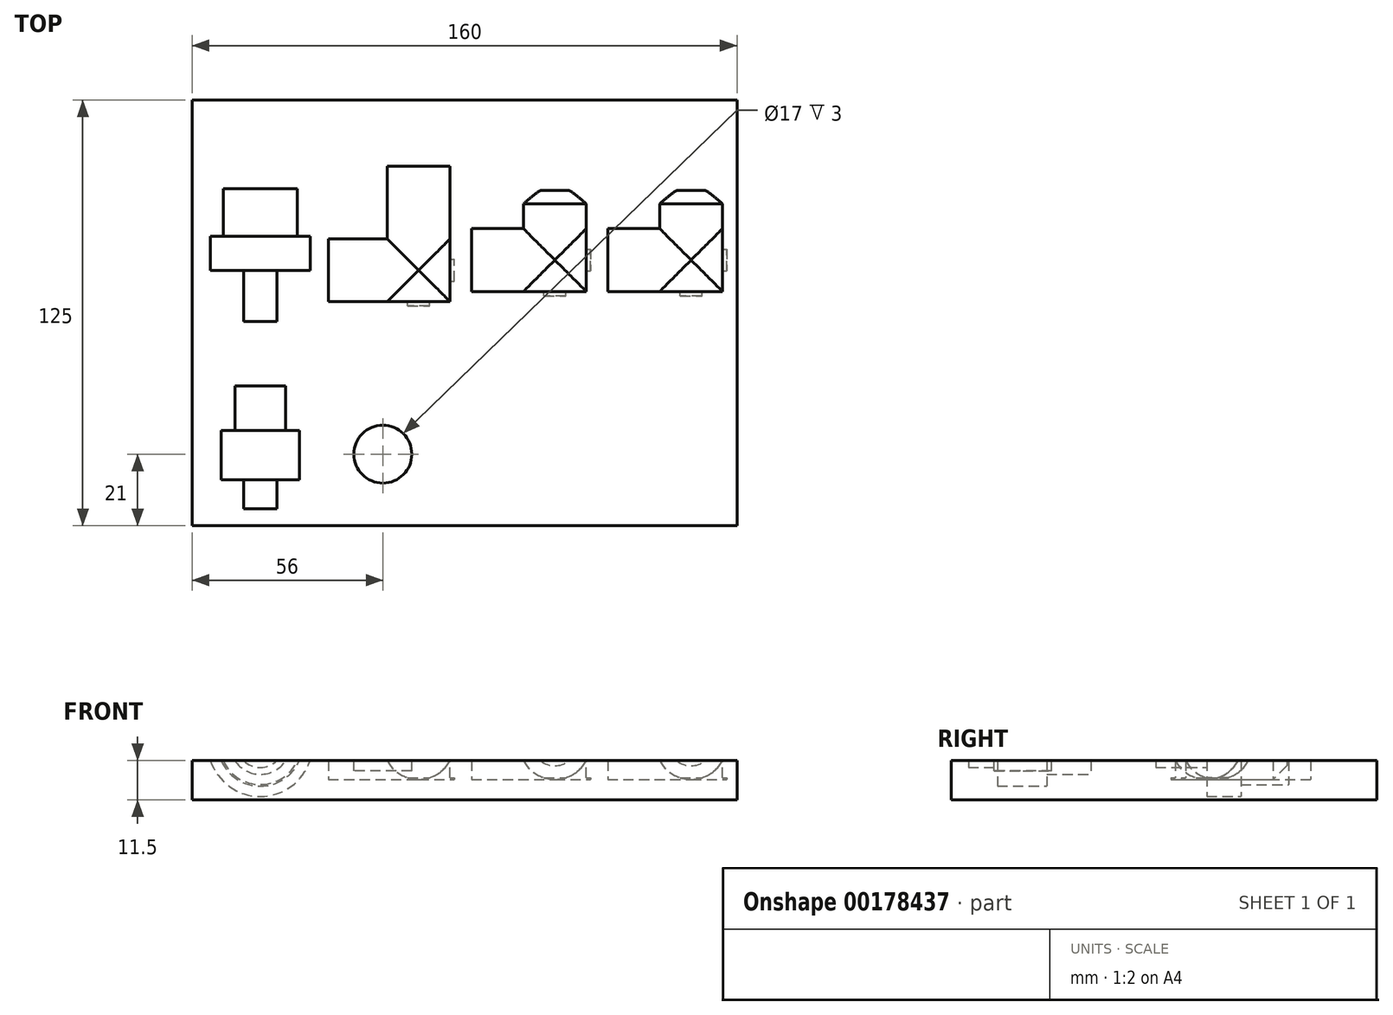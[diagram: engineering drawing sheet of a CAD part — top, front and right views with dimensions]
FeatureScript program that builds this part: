
annotation { "Feature Type Name" : "Feature", "Feature Type Description" : "" }
export const myFeature = defineFeature(function(context is Context, id is Id, definition is map)
    precondition{}
    {
        {
            var Q0;
            Q0=qCreatedBy(makeId("Top.planeOp"),FACE);
            var sketch = newSketch(context, id + "F0", { "sketchPlane" : qUnion([Q0])});
            skLineSegment(sketch, "E0.bottom", {"start": v(0, 0) * mm, "end": v(160, 0) * mm});
            skLineSegment(sketch, "E0.top", {"start": v(0, 125) * mm, "end": v(160, 125) * mm});
            skLineSegment(sketch, "E0.left", {"start": v(0, 0) * mm, "end": v(0, 125) * mm});
            skLineSegment(sketch, "E0.right", {"start": v(160, 0) * mm, "end": v(160, 125) * mm});
            skSolve(sketch);
        }
        {
            var Q0;
            Q0=makeQuery(id+"F0.imprint","IMPRINT",FACE,{"disambiguationData":[TD([[makeQuery(id+"F0.imprint","IMPRINT",EDGE,{"derivedFrom":sQuery(id+"F0.wireOp",EDGE,"E0.bottom")}),1.0]])]});
            extrude(context, id + "F1", {"entities" : qUnion([Q0]), "oppositeDirection" : true, "depth" : 16.5 * mm});
        }
        {
            var Q0;
            Q0=makeQuery(id+"F1.opExtrude","CAP_FACE",FACE,{"disambiguationData":[OSD([sQuery(id+"F0.wireOp",EDGE,"E0.bottom"),sQuery(id+"F0.wireOp",EDGE,"E0.top"),sQuery(id+"F0.wireOp",EDGE,"E0.left"),sQuery(id+"F0.wireOp",EDGE,"E0.right")])],"isStart":true});
            var sketch = newSketch(context, id + "F2", { "sketchPlane" : qUnion([Q0])});
            skLineSegment(sketch, "E1.bottom", {"start": v(0, 0) * mm, "end": v(20, 0) * mm, "construction": true});
            skLineSegment(sketch, "E1.top", {"start": v(0, 60) * mm, "end": v(20, 60) * mm, "construction": true});
            skLineSegment(sketch, "E1.left", {"start": v(0, 0) * mm, "end": v(0, 60) * mm, "construction": true});
            skLineSegment(sketch, "E1.right", {"start": v(20, 0) * mm, "end": v(20, 60) * mm, "construction": true});
            skLineSegment(sketch, "E2.bottom", {"start": v(20, 60) * mm, "end": v(27, 60) * mm});
            skLineSegment(sketch, "E2.left", {"start": v(20, 60) * mm, "end": v(20, 75) * mm});
            skLineSegment(sketch, "E2.right", {"start": v(27, 60) * mm, "end": v(27, 75) * mm});
            skLineSegment(sketch, "E3.bottom", {"start": v(27, 75) * mm, "end": v(35.5, 75) * mm});
            skLineSegment(sketch, "E3.top", {"start": v(32, 85) * mm, "end": v(35.5, 85) * mm});
            skLineSegment(sketch, "E3.left", {"start": v(20, 75) * mm, "end": v(20, 85) * mm});
            skLineSegment(sketch, "E3.right", {"start": v(35.5, 75) * mm, "end": v(35.5, 85) * mm});
            skLineSegment(sketch, "E4.top", {"start": v(24.5, 99) * mm, "end": v(32, 99) * mm});
            skLineSegment(sketch, "E4.left", {"start": v(20, 85) * mm, "end": v(20, 99) * mm});
            skLineSegment(sketch, "E4.right", {"start": v(32, 85) * mm, "end": v(32, 99) * mm});
            skLineSegment(sketch, "E5.top", {"start": v(20, 113) * mm, "end": v(24.5, 113) * mm});
            skLineSegment(sketch, "E5.left", {"start": v(20, 99) * mm, "end": v(20, 113) * mm});
            skLineSegment(sketch, "E5.right", {"start": v(24.5, 99) * mm, "end": v(24.5, 113) * mm});
            skSolve(sketch);
        }
        {
            var Q0;
            Q0=qSketchRegion(id+"F2",true);
            var Q1;
            Q1=sQuery(id+"F2.wireOp",EDGE,"E4.left");
            revolve(context, id + "F3", {"operationType" : NewBodyOperationType.REMOVE, "entities" : qUnion([Q0]), "axis" : qUnion([Q1]), "revolveType" : RevolveType.FULL, "oppositeDirection" : true});
        }
        {
            var Q0;
            Q0=makeQuery(id+"F1.opExtrude","CAP_FACE",FACE,{"disambiguationData":[OSD([sQuery(id+"F0.wireOp",EDGE,"E0.bottom"),sQuery(id+"F0.wireOp",EDGE,"E0.top"),sQuery(id+"F0.wireOp",EDGE,"E0.left"),sQuery(id+"F0.wireOp",EDGE,"E0.right")])],"isStart":true});
            var sketch = newSketch(context, id + "F4", { "sketchPlane" : qUnion([Q0])});
            skLineSegment(sketch, "E6.bottom", {"start": v(0, 0) * mm, "end": v(40, 0) * mm, "construction": true});
            skLineSegment(sketch, "E6.top", {"start": v(0, 75) * mm, "end": v(40, 75) * mm, "construction": true});
            skLineSegment(sketch, "E6.left", {"start": v(0, 0) * mm, "end": v(0, 75) * mm, "construction": true});
            skLineSegment(sketch, "E6.right", {"start": v(40, 0) * mm, "end": v(40, 75) * mm, "construction": true});
            skPoint(sketch, "E7.oppositeSnap0", {"position": v(31, 64.5) * mm});
            skLineSegment(sketch, "E7.bottom", {"start": v(40, 75) * mm, "end": v(77, 75) * mm});
            skLineSegment(sketch, "E7.top", {"start": v(40, 64.5) * mm, "end": v(77, 64.5) * mm});
            skLineSegment(sketch, "E7.left", {"start": v(40, 75) * mm, "end": v(40, 64.5) * mm});
            skLineSegment(sketch, "E7.right", {"start": v(77, 75) * mm, "end": v(77, 64.5) * mm});
            skSolve(sketch);
        }
        {
            var Q0;
            Q0=makeQuery(id+"F4.imprint","IMPRINT",FACE,{"disambiguationData":[TD([[makeQuery(id+"F4.imprint","IMPRINT",EDGE,{"derivedFrom":sQuery(id+"F4.wireOp",EDGE,"E7.bottom")}),-1.0]])]});
            var Q1;
            Q1=sQuery(id+"F4.wireOp",EDGE,"E7.bottom");
            revolve(context, id + "F5", {"operationType" : NewBodyOperationType.REMOVE, "entities" : qUnion([Q0]), "axis" : qUnion([Q1]), "revolveType" : RevolveType.FULL, "oppositeDirection" : true});
        }
        {
            var Q0;
            Q0=makeQuery(id+"F1.opExtrude","CAP_FACE",FACE,{"disambiguationData":[OSD([sQuery(id+"F0.wireOp",EDGE,"E0.bottom"),sQuery(id+"F0.wireOp",EDGE,"E0.top"),sQuery(id+"F0.wireOp",EDGE,"E0.left"),sQuery(id+"F0.wireOp",EDGE,"E0.right")])],"isStart":true});
            var sketch = newSketch(context, id + "F6", { "sketchPlane" : qUnion([Q0])});
            skLineSegment(sketch, "E8.bottom", {"start": v(77, 64.5) * mm, "end": v(66.5, 64.5) * mm});
            skLineSegment(sketch, "E8.top", {"start": v(77, 105.5) * mm, "end": v(66.5, 105.5) * mm});
            skLineSegment(sketch, "E8.left", {"start": v(77, 64.5) * mm, "end": v(77, 105.5) * mm});
            skLineSegment(sketch, "E8.right", {"start": v(66.5, 64.5) * mm, "end": v(66.5, 105.5) * mm});
            skSolve(sketch);
        }
        {
            var Q0;
            {var subQ0=sQuery(id+"F6.wireOp",EDGE,"E8.top");Q0=makeQuery(id+"F6.imprint","IMPRINT",FACE,{"disambiguationData":[TD([[makeQuery(id+"F6.imprint","IMPRINT",EDGE,{"derivedFrom":subQ0}),1.0]])]});}
            var Q1;
            {var subQ0=sQuery(id+"F6.wireOp",EDGE,"E8.bottom");Q1=makeQuery(id+"F6.imprint","IMPRINT",FACE,{"disambiguationData":[TD([[makeQuery(id+"F6.imprint","IMPRINT",EDGE,{"derivedFrom":subQ0}),-1.0]])]});}
            var Q2;
            Q2=sQuery(id+"F6.wireOp",EDGE,"E8.right");
            revolve(context, id + "F7", {"operationType" : NewBodyOperationType.REMOVE, "entities" : qUnion([Q0, Q1]), "axis" : qUnion([Q2]), "revolveType" : RevolveType.FULL, "oppositeDirection" : true});
        }
        {
            var Q0;
            Q0=makeQuery(id+"F1.opExtrude","CAP_FACE",FACE,{"disambiguationData":[OSD([sQuery(id+"F0.wireOp",EDGE,"E0.bottom"),sQuery(id+"F0.wireOp",EDGE,"E0.top"),sQuery(id+"F0.wireOp",EDGE,"E0.left"),sQuery(id+"F0.wireOp",EDGE,"E0.right")])],"isStart":true});
            var sketch = newSketch(context, id + "F8", { "sketchPlane" : qUnion([Q0])});
            skLineSegment(sketch, "E9.bottom", {"start": v(77, 64.5) * mm, "end": v(82, 64.5) * mm, "construction": true});
            skLineSegment(sketch, "E9.top", {"start": v(77, 67.5) * mm, "end": v(82, 67.5) * mm, "construction": true});
            skLineSegment(sketch, "E9.left", {"start": v(77, 64.5) * mm, "end": v(77, 67.5) * mm, "construction": true});
            skLineSegment(sketch, "E9.right", {"start": v(82, 64.5) * mm, "end": v(82, 67.5) * mm, "construction": true});
            skLineSegment(sketch, "E10.bottom", {"start": v(82, 67.5) * mm, "end": v(117, 67.5) * mm});
            skLineSegment(sketch, "E10.top", {"start": v(82, 78) * mm, "end": v(117, 78) * mm});
            skLineSegment(sketch, "E10.left", {"start": v(82, 67.5) * mm, "end": v(82, 78) * mm});
            skLineSegment(sketch, "E10.right", {"start": v(117, 67.5) * mm, "end": v(117, 78) * mm});
            skLineSegment(sketch, "E11", {"start": v(117, 67.5) * mm, "end": v(122, 67.5) * mm, "construction": true});
            skLineSegment(sketch, "E12.bottom", {"start": v(122, 67.5) * mm, "end": v(157, 67.5) * mm});
            skLineSegment(sketch, "E12.top", {"start": v(122, 78) * mm, "end": v(157, 78) * mm});
            skLineSegment(sketch, "E12.left", {"start": v(122, 67.5) * mm, "end": v(122, 78) * mm});
            skLineSegment(sketch, "E12.right", {"start": v(157, 67.5) * mm, "end": v(157, 78) * mm});
            skSolve(sketch);
        }
        {
            var Q0;
            Q0=makeQuery(id+"F8.imprint","IMPRINT",FACE,{"disambiguationData":[TD([[makeQuery(id+"F8.imprint","IMPRINT",EDGE,{"derivedFrom":sQuery(id+"F8.wireOp",EDGE,"E10.bottom")}),1.0]])]});
            var Q1;
            Q1=makeQuery(id+"F8.imprint","IMPRINT",FACE,{"disambiguationData":[TD([[makeQuery(id+"F8.imprint","IMPRINT",EDGE,{"derivedFrom":sQuery(id+"F8.wireOp",EDGE,"E12.bottom")}),1.0]])]});
            var Q2;
            Q2=sQuery(id+"F8.wireOp",EDGE,"E10.top");
            revolve(context, id + "F9", {"operationType" : NewBodyOperationType.REMOVE, "entities" : qUnion([Q0, Q1]), "axis" : qUnion([Q2]), "revolveType" : RevolveType.FULL, "oppositeDirection" : true});
        }
        {
            var Q0;
            Q0=makeQuery(id+"F1.opExtrude","CAP_FACE",FACE,{"disambiguationData":[OSD([sQuery(id+"F0.wireOp",EDGE,"E0.bottom"),sQuery(id+"F0.wireOp",EDGE,"E0.top"),sQuery(id+"F0.wireOp",EDGE,"E0.left"),sQuery(id+"F0.wireOp",EDGE,"E0.right")])],"isStart":true});
            var sketch = newSketch(context, id + "F10", { "sketchPlane" : qUnion([Q0])});
            skLineSegment(sketch, "E13.bottom", {"start": v(117, 67.5) * mm, "end": v(106.5, 67.5) * mm});
            skLineSegment(sketch, "E13.top", {"start": v(113, 98.5) * mm, "end": v(106.5, 98.5) * mm});
            skLineSegment(sketch, "E13.left", {"start": v(117, 67.5) * mm, "end": v(117, 94.5) * mm});
            skLineSegment(sketch, "E13.right", {"start": v(106.5, 67.5) * mm, "end": v(106.5, 98.5) * mm});
            skLineSegment(sketch, "E14", {"start": v(117, 67.5) * mm, "end": v(117, 94.5) * mm, "construction": true});
            skLineSegment(sketch, "E15", {"start": v(117, 94.5) * mm, "end": v(113, 98.5) * mm});
            skSolve(sketch);
        }
        {
            var Q0;
            {var subQ5=sQuery(id+"F10.wireOp",EDGE,"E13.top");Q0=makeQuery(id+"F10.imprint","IMPRINT",FACE,{"disambiguationData":[TD([[makeQuery(id+"F10.imprint","IMPRINT",EDGE,{"derivedFrom":subQ5}),1.0]])]});}
            var Q1;
            {var subQ0=sQuery(id+"F10.wireOp",EDGE,"E13.bottom");Q1=makeQuery(id+"F10.imprint","IMPRINT",FACE,{"disambiguationData":[TD([[makeQuery(id+"F10.imprint","IMPRINT",EDGE,{"derivedFrom":subQ0}),-1.0]])]});}
            var Q2;
            Q2=sQuery(id+"F10.wireOp",EDGE,"E13.right");
            revolve(context, id + "F11", {"operationType" : NewBodyOperationType.REMOVE, "entities" : qUnion([Q0, Q1]), "axis" : qUnion([Q2]), "revolveType" : RevolveType.FULL, "oppositeDirection" : true});
        }
        {
            var Q0;
            Q0=makeQuery(id+"F1.opExtrude","CAP_FACE",FACE,{"disambiguationData":[OSD([sQuery(id+"F0.wireOp",EDGE,"E0.bottom"),sQuery(id+"F0.wireOp",EDGE,"E0.top"),sQuery(id+"F0.wireOp",EDGE,"E0.left"),sQuery(id+"F0.wireOp",EDGE,"E0.right")])],"isStart":true});
            var sketch = newSketch(context, id + "F12", { "sketchPlane" : qUnion([Q0])});
            skLineSegment(sketch, "E16.bottom", {"start": v(157, 67.5) * mm, "end": v(146.5, 67.5) * mm});
            skLineSegment(sketch, "E16.top", {"start": v(153, 98.5) * mm, "end": v(146.5, 98.5) * mm});
            skLineSegment(sketch, "E16.left", {"start": v(157, 67.5) * mm, "end": v(157, 94.5) * mm});
            skLineSegment(sketch, "E16.right", {"start": v(146.5, 67.5) * mm, "end": v(146.5, 98.5) * mm});
            skLineSegment(sketch, "E17", {"start": v(157, 67.5) * mm, "end": v(157, 94.5) * mm, "construction": true});
            skLineSegment(sketch, "E18", {"start": v(157, 94.5) * mm, "end": v(153, 98.5) * mm});
            skSolve(sketch);
        }
        {
            var Q0;
            {var subQ2=sQuery(id+"F12.wireOp",EDGE,"E16.top");Q0=makeQuery(id+"F12.imprint","IMPRINT",FACE,{"disambiguationData":[TD([[makeQuery(id+"F12.imprint","IMPRINT",EDGE,{"derivedFrom":subQ2}),1.0]])]});}
            var Q1;
            {var subQ0=sQuery(id+"F12.wireOp",EDGE,"E16.bottom");Q1=makeQuery(id+"F12.imprint","IMPRINT",FACE,{"disambiguationData":[TD([[makeQuery(id+"F12.imprint","IMPRINT",EDGE,{"derivedFrom":subQ0}),-1.0]])]});}
            var Q2;
            Q2=sQuery(id+"F12.wireOp",EDGE,"E16.right");
            revolve(context, id + "F13", {"operationType" : NewBodyOperationType.REMOVE, "entities" : qUnion([Q0, Q1]), "axis" : qUnion([Q2]), "revolveType" : RevolveType.FULL, "oppositeDirection" : true});
        }
        {
            var Q0;
            Q0=makeQuery(id+"F1.opExtrude","CAP_FACE",FACE,{"disambiguationData":[OSD([sQuery(id+"F0.wireOp",EDGE,"E0.bottom"),sQuery(id+"F0.wireOp",EDGE,"E0.top"),sQuery(id+"F0.wireOp",EDGE,"E0.left"),sQuery(id+"F0.wireOp",EDGE,"E0.right")])],"isStart":true});
            var sketch = newSketch(context, id + "F14", { "sketchPlane" : qUnion([Q0])});
            skLineSegment(sketch, "E19.bottom", {"start": v(0, 0) * mm, "end": v(20, 0) * mm, "construction": true});
            skLineSegment(sketch, "E19.top", {"start": v(0, 5) * mm, "end": v(20, 5) * mm, "construction": true});
            skLineSegment(sketch, "E19.left", {"start": v(0, 0) * mm, "end": v(0, 5) * mm, "construction": true});
            skLineSegment(sketch, "E19.right", {"start": v(20, 0) * mm, "end": v(20, 5) * mm, "construction": true});
            skLineSegment(sketch, "E20.bottom", {"start": v(20, 5) * mm, "end": v(27, 5) * mm});
            skLineSegment(sketch, "E20.left", {"start": v(20, 5) * mm, "end": v(20, 13.5) * mm});
            skLineSegment(sketch, "E20.right", {"start": v(27, 5) * mm, "end": v(27, 13.5) * mm});
            skLineSegment(sketch, "E21.bottom", {"start": v(27, 13.5) * mm, "end": v(32.5, 13.5) * mm});
            skLineSegment(sketch, "E21.top", {"start": v(29, 28) * mm, "end": v(32.5, 28) * mm});
            skLineSegment(sketch, "E21.left", {"start": v(20, 13.5) * mm, "end": v(20, 28) * mm});
            skLineSegment(sketch, "E21.right", {"start": v(32.5, 13.5) * mm, "end": v(32.5, 28) * mm});
            skLineSegment(sketch, "E22.top", {"start": v(20, 41) * mm, "end": v(29, 41) * mm});
            skLineSegment(sketch, "E22.left", {"start": v(20, 28) * mm, "end": v(20, 41) * mm});
            skLineSegment(sketch, "E22.right", {"start": v(29, 28) * mm, "end": v(29, 41) * mm});
            skSolve(sketch);
        }
        {
            var Q0;
            Q0=makeQuery(id+"F14.imprint","IMPRINT",FACE,{"disambiguationData":[TD([[makeQuery(id+"F14.imprint","IMPRINT",EDGE,{"derivedFrom":sQuery(id+"F14.wireOp",EDGE,"E20.bottom")}),1.0]])]});
            var Q1;
            Q1=sQuery(id+"F14.wireOp",EDGE,"E21.left");
            revolve(context, id + "F15", {"operationType" : NewBodyOperationType.REMOVE, "entities" : qUnion([Q0]), "axis" : qUnion([Q1]), "revolveType" : RevolveType.FULL, "oppositeDirection" : true});
        }
        {
            var Q0;
            Q0=makeQuery(id+"F1.opExtrude","CAP_FACE",FACE,{"disambiguationData":[OSD([sQuery(id+"F0.wireOp",EDGE,"E0.bottom"),sQuery(id+"F0.wireOp",EDGE,"E0.top"),sQuery(id+"F0.wireOp",EDGE,"E0.left"),sQuery(id+"F0.wireOp",EDGE,"E0.right")])],"isStart":true});
            var sketch = newSketch(context, id + "F16", { "sketchPlane" : qUnion([Q0])});
            skLineSegment(sketch, "E23.bottom", {"start": v(0, 0) * mm, "end": v(56, 0) * mm, "construction": true});
            skLineSegment(sketch, "E23.top", {"start": v(0, 21) * mm, "end": v(56, 21) * mm, "construction": true});
            skLineSegment(sketch, "E23.left", {"start": v(0, 0) * mm, "end": v(0, 21) * mm, "construction": true});
            skLineSegment(sketch, "E23.right", {"start": v(56, 0) * mm, "end": v(56, 21) * mm, "construction": true});
            skCircle(sketch, "E24", {"center": v(56, 21) * mm, "radius": 8.5 * mm});
            skSolve(sketch);
        }
        {
            var Q0;
            Q0=makeQuery(id+"F16.imprint","IMPRINT",FACE,{"disambiguationData":[TD([[makeQuery(id+"F16.imprint","IMPRINT",EDGE,{"derivedFrom":sQuery(id+"F16.wireOp",EDGE,"E24")}),1.0]])]});
            extrude(context, id + "F17", {"entities" : qUnion([Q0]), "operationType" : NewBodyOperationType.REMOVE, "oppositeDirection" : true, "depth" : 8 * mm});
        }
        {
            var Q0;
            Q0=makeQuery(id+"F1.opExtrude","SWEPT_FACE",FACE,{"disambiguationData":[OSD([sQuery(id+"F0.wireOp",EDGE,"E0.bottom")])]});
            var sketch = newSketch(context, id + "F18", { "sketchPlane" : qUnion([Q0])});
            skLineSegment(sketch, "E25.bottom", {"start": v(0, 0) * mm, "end": v(160, 0) * mm});
            skLineSegment(sketch, "E25.top", {"start": v(0, -5) * mm, "end": v(160, -5) * mm});
            skLineSegment(sketch, "E25.left", {"start": v(0, 0) * mm, "end": v(0, -5) * mm});
            skLineSegment(sketch, "E25.right", {"start": v(160, 0) * mm, "end": v(160, -5) * mm});
            skSolve(sketch);
        }
        {
            var Q0;
            Q0=makeQuery(id+"F18.imprint","IMPRINT",FACE,{"disambiguationData":[TD([[makeQuery(id+"F18.imprint","IMPRINT",EDGE,{"derivedFrom":sQuery(id+"F18.wireOp",EDGE,"E25.bottom")}),-1.0]])]});
            extrude(context, id + "F19", {"entities" : qUnion([Q0]), "operationType" : NewBodyOperationType.REMOVE, "oppositeDirection" : true, "depth" : 160 * mm});
        }
        {
            var Q0;
            Q0=makeQuery(id+"F19.boolean.opBoolean","COPY",FACE,{"derivedFrom":makeQuery(id+"F19.opExtrude","SWEPT_FACE",FACE,{"disambiguationData":[OSD([sQuery(id+"F18.wireOp",EDGE,"E25.top")])]})});
            var sketch = newSketch(context, id + "F20", { "sketchPlane" : qUnion([Q0])});
            skLineSegment(sketch, "E26.bottom", {"start": v(57.27, 65.77) * mm, "end": v(75.73, 65.77) * mm});
            skLineSegment(sketch, "E26.top", {"start": v(57.27, 64.5) * mm, "end": v(75.73, 64.5) * mm});
            skLineSegment(sketch, "E26.left", {"start": v(57.27, 65.77) * mm, "end": v(57.27, 64.5) * mm});
            skLineSegment(sketch, "E26.right", {"start": v(75.73, 65.77) * mm, "end": v(75.73, 64.5) * mm});
            skLineSegment(sketch, "E27.bottom", {"start": v(77, 65.77) * mm, "end": v(75.73, 65.77) * mm});
            skLineSegment(sketch, "E27.top", {"start": v(77, 84.23) * mm, "end": v(75.73, 84.23) * mm});
            skLineSegment(sketch, "E27.left", {"start": v(77, 65.77) * mm, "end": v(77, 84.23) * mm});
            skLineSegment(sketch, "E27.right", {"start": v(75.73, 65.77) * mm, "end": v(75.73, 84.23) * mm});
            skLineSegment(sketch, "E28.bottom", {"start": v(97.27, 68.77) * mm, "end": v(115.73, 68.77) * mm});
            skLineSegment(sketch, "E28.top", {"start": v(97.27, 67.5) * mm, "end": v(115.73, 67.5) * mm});
            skLineSegment(sketch, "E28.left", {"start": v(97.27, 68.77) * mm, "end": v(97.27, 67.5) * mm});
            skLineSegment(sketch, "E28.right", {"start": v(115.73, 68.77) * mm, "end": v(115.73, 67.5) * mm});
            skLineSegment(sketch, "E29.bottom", {"start": v(117, 68.77) * mm, "end": v(115.73, 68.77) * mm});
            skLineSegment(sketch, "E29.top", {"start": v(117, 87.23) * mm, "end": v(115.73, 87.23) * mm});
            skLineSegment(sketch, "E29.left", {"start": v(117, 68.77) * mm, "end": v(117, 87.23) * mm});
            skLineSegment(sketch, "E29.right", {"start": v(115.73, 68.77) * mm, "end": v(115.73, 87.23) * mm});
            skLineSegment(sketch, "E30.bottom", {"start": v(137.27, 68.77) * mm, "end": v(155.73, 68.77) * mm});
            skLineSegment(sketch, "E30.top", {"start": v(137.27, 67.5) * mm, "end": v(155.73, 67.5) * mm});
            skLineSegment(sketch, "E30.left", {"start": v(137.27, 68.77) * mm, "end": v(137.27, 67.5) * mm});
            skLineSegment(sketch, "E30.right", {"start": v(155.73, 68.77) * mm, "end": v(155.73, 67.5) * mm});
            skLineSegment(sketch, "E31.bottom", {"start": v(157, 68.77) * mm, "end": v(155.73, 68.77) * mm});
            skLineSegment(sketch, "E31.top", {"start": v(157, 87.23) * mm, "end": v(155.73, 87.23) * mm});
            skLineSegment(sketch, "E31.left", {"start": v(157, 68.77) * mm, "end": v(157, 87.23) * mm});
            skLineSegment(sketch, "E31.right", {"start": v(155.73, 68.77) * mm, "end": v(155.73, 87.23) * mm});
            skSolve(sketch);
        }
        {
            var Q0;
            Q0 = qSketchRegion(id + "F20", true);
            extrude(context, id + "F21", {"entities" : qUnion([Q0]), "operationType" : NewBodyOperationType.ADD, "oppositeDirection" : true, "depth" : 5 * mm});
        }
    });
